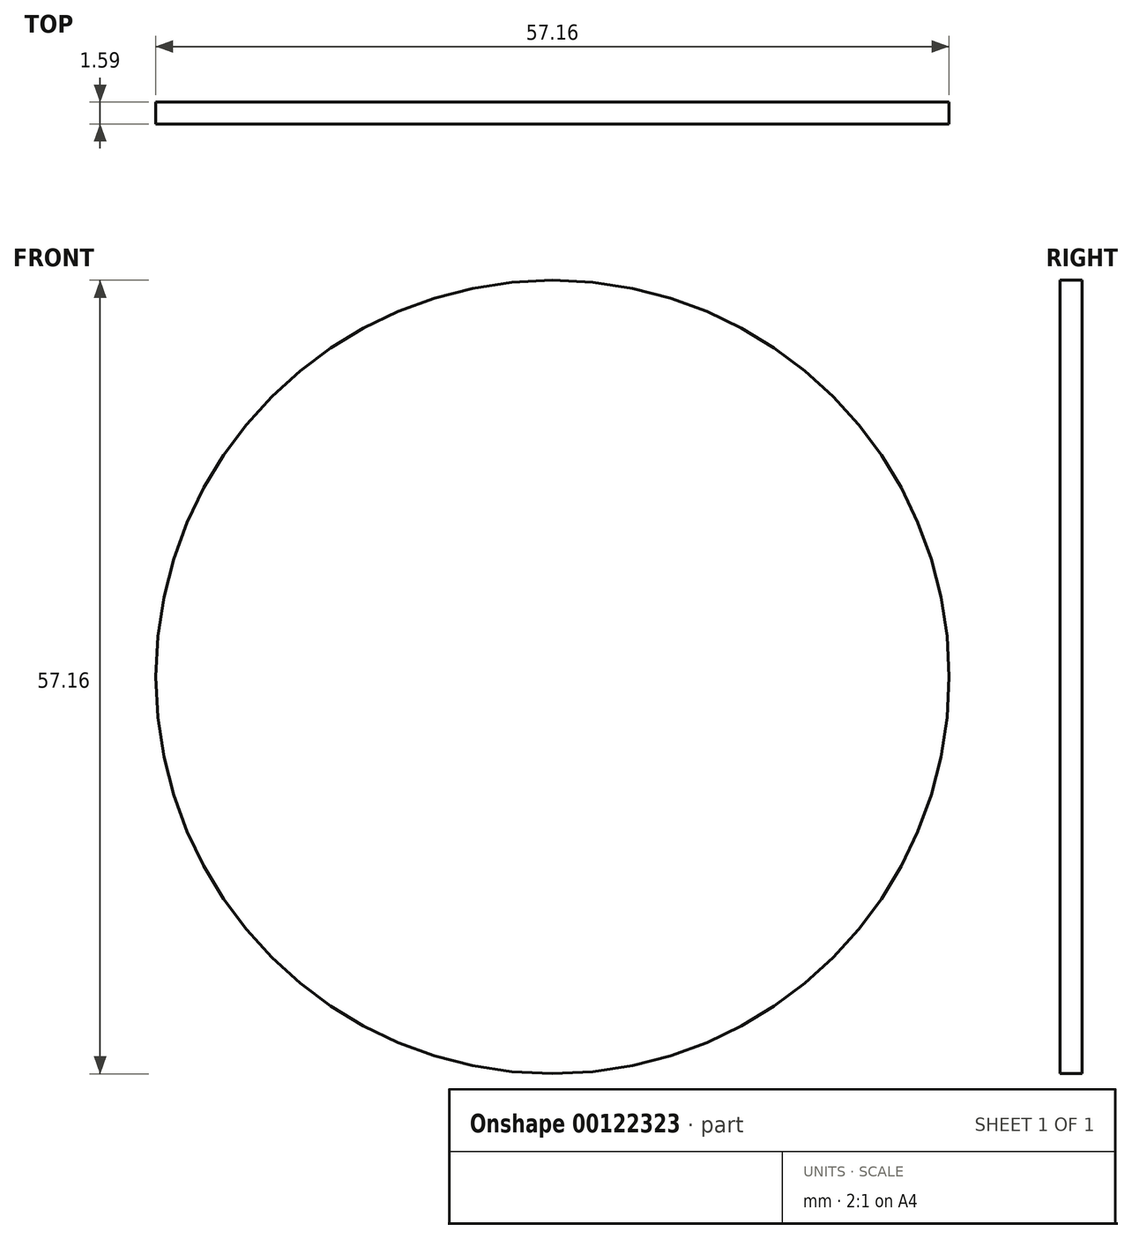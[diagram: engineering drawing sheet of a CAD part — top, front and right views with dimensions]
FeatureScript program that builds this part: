
annotation { "Feature Type Name" : "Feature", "Feature Type Description" : "" }
export const myFeature = defineFeature(function(context is Context, id is Id, definition is map)
    precondition{}
    {
        {
            var Q0;
            Q0=qCreatedBy(makeId("Front.planeOp"),FACE);
            var sketch = newSketch(context, id + "F0", { "sketchPlane" : qUnion([Q0])});
            skCircle(sketch, "E0", {"center": v(0, 0) * mm, "radius": 28.57 * mm});
            skSolve(sketch);
        }
        {
            var Q0;
            Q0=makeQuery(id+"F0.imprint","IMPRINT",FACE,{"disambiguationData":[TD([[makeQuery(id+"F0.imprint","IMPRINT",EDGE,{"derivedFrom":sQuery(id+"F0.wireOp",EDGE,"E0")}),1.0]])]});
            extrude(context, id + "F1", {"entities" : qUnion([Q0]), "depth" : 1.59 * mm});
        }
    });
